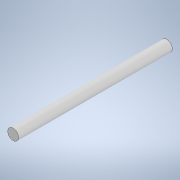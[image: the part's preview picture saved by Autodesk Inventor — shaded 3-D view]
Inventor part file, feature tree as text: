
AUTODESK INVENTOR PART (.ipt)
format: ipt  version: 2021 (Build 250183000, 183)  size: 91,648 bytes
history: native  units: mm
features: extrude x1, sketch x1
ambient origin geometry x8: Origin, YZ Plane, XZ Plane, XY Plane, X Axis, Y Axis, Z Axis, Center Point
bodies: Solid1 (feature_tree)
feature tree (2):
  extrude  "Extrusion1"  Depth=42.5mm TaperAngle=0.0deg
  sketch  "Sketch1"  dims[d0=3.0mm d1=42.5mm d2=0.0mm]
